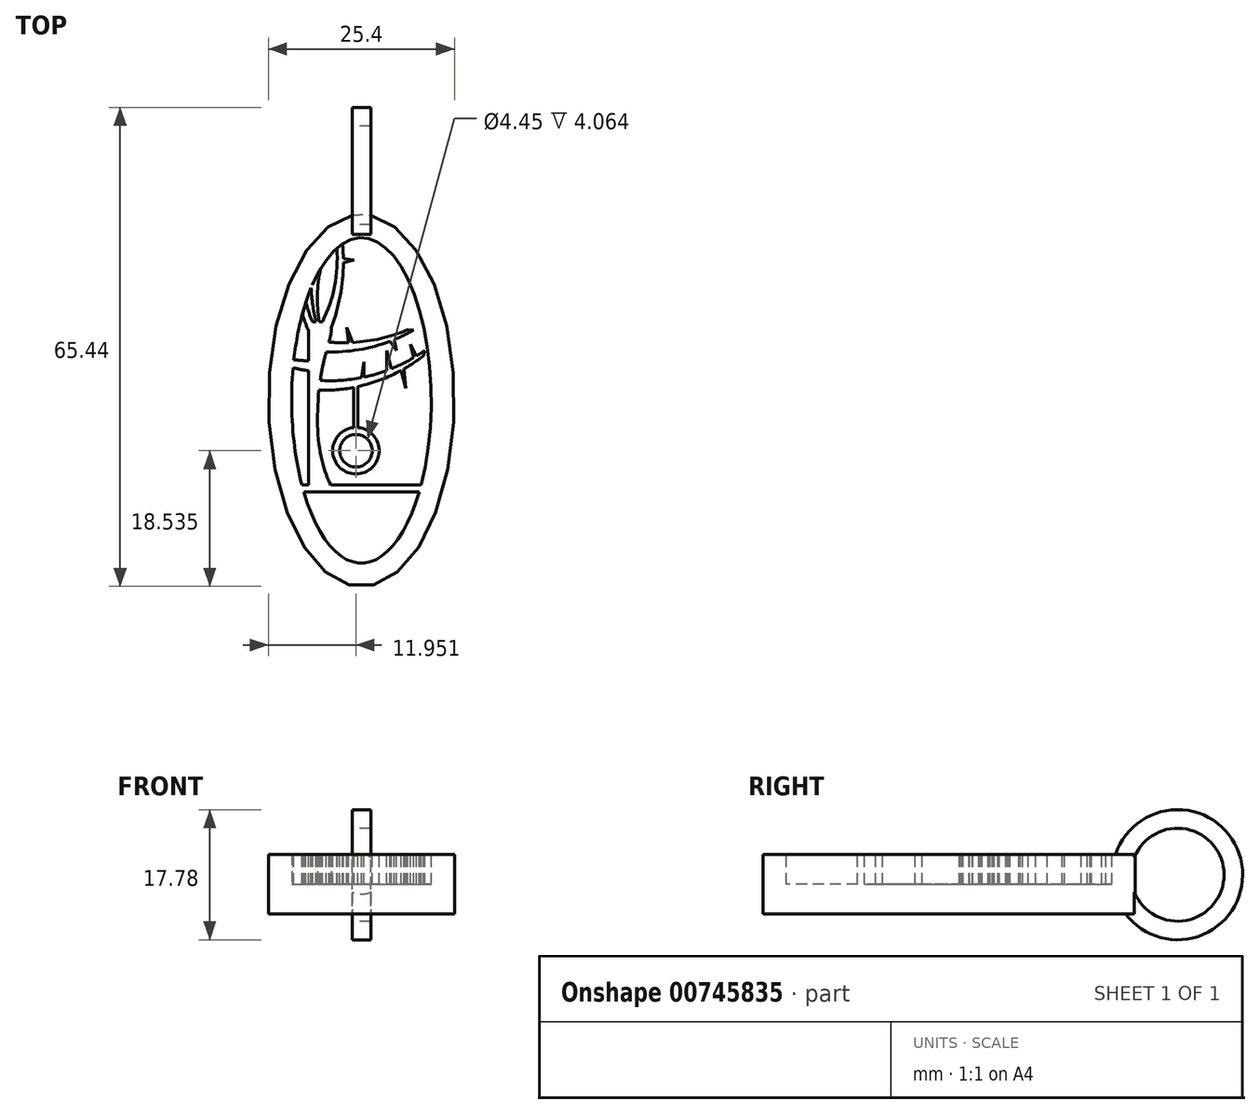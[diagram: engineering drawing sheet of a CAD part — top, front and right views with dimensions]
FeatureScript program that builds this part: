
annotation { "Feature Type Name" : "Feature", "Feature Type Description" : "" }
export const myFeature = defineFeature(function(context is Context, id is Id, definition is map)
    precondition{}
    {
        {
            var Q0;
            Q0=qCreatedBy(makeId("Top.planeOp"),FACE);
            var sketch = newSketch(context, id + "F0", { "sketchPlane" : qUnion([Q0])});
            skEllipse(sketch, "E0", {"center": v(0, 0) * mm, "majorRadius": 25.4 * mm, "minorRadius": 12.7 * mm, "majorAxis": v(0, 1)});
            skSolve(sketch);
        }
        {
            var Q0;
            Q0=qSketchRegion(id+"F0",true);
            extrude(context, id + "F1", {"entities" : qUnion([Q0]), "endBound" : BoundingType.SYMMETRIC, "depth" : 8.13 * mm, "offsetDistance" : 25.4 * mm});
        }
        {
            var Q0;
            Q0=makeQuery(id+"F1.opExtrude","CAP_FACE",FACE,{"disambiguationData":[OSD([sQuery(id+"F0.wireOp",EDGE,"E0")])],"isStart":false});
            var sketch = newSketch(context, id + "F2", { "sketchPlane" : qUnion([Q0])});
            skEllipse(sketch, "E1", {"center": v(0, 0) * mm, "majorRadius": 22.23 * mm, "minorRadius": 9.53 * mm, "majorAxis": v(0, 1)});
            skSolve(sketch);
        }
        {
            var Q0;
            Q0=qSketchRegion(id+"F2",true);
            extrude(context, id + "F3", {"entities" : qUnion([Q0]), "operationType" : NewBodyOperationType.REMOVE, "oppositeDirection" : true, "depth" : 4.06 * mm, "offsetDistance" : 25.4 * mm});
        }
        {
            var Q0;
            Q0=makeQuery(id+"F2.imprint","IMPRINT",FACE,{"disambiguationData":[TD([[makeQuery(id+"F2.imprint","IMPRINT",EDGE,{"derivedFrom":sQuery(id+"F2.wireOp",EDGE,"E1")}),1.0]])]});
            var sketch = newSketch(context, id + "F4", { "sketchPlane" : qUnion([Q0])});
            skLineSegment(sketch, "E2", {"start": v(-7.24, 10.97) * mm, "end": v(-7.24, -11.57) * mm});
            skLineSegment(sketch, "E3", {"start": v(-7.24, -11.57) * mm, "end": v(-4.2, -11.57) * mm});
            skFitSpline(sketch, "E4", {"points": [v(-4.2, -11.57) * mm, v(-5.85, -5.45) * mm, v(-4.99, 5.96) * mm, v(-4.5, 10.63) * mm, v(-7.24, 10.97) * mm], "startDerivative": vector(-8.16, 15.39) * mm, "endDerivative": vector(-7.14, 8.4) * mm});
            skLineSegment(sketch, "E5", {"start": v(-5.8, -18.4) * mm, "end": v(-5.71, -17.72) * mm});
            skLineSegment(sketch, "E6", {"start": v(-8.52, -11.57) * mm, "end": v(8.47, -11.57) * mm});
            skLineSegment(sketch, "E7", {"start": v(-8.52, -11.57) * mm, "end": v(-8.19, -12.52) * mm});
            skLineSegment(sketch, "E8", {"start": v(-8.19, -12.52) * mm, "end": v(8.37, -12.52) * mm});
            skLineSegment(sketch, "E9", {"start": v(8.37, -12.52) * mm, "end": v(8.47, -11.57) * mm});
            skPoint(sketch, "E10", {"position": v(-5.79, 1.4) * mm});
            skLineSegment(sketch, "E11", {"start": v(-0.49, 2.6) * mm, "end": v(-0.46, -4.66) * mm});
            skLineSegment(sketch, "E12", {"start": v(-1.04, -4.66) * mm, "end": v(-1.04, 2.05) * mm});
            skCircle(sketch, "E13", {"center": v(-0.75, -6.86) * mm, "radius": 3.18 * mm});
            skPoint(sketch, "E13.third.point", {"position": v(0.65, -9.72) * mm});
            skCircle(sketch, "E14", {"center": v(-0.75, -6.86) * mm, "radius": 2.22 * mm});
            skArc(sketch, "E15", {"start": v(-5.79, 1.4) * mm, "mid": v(1.75, 2.5) * mm, "end": v(8.47, 6.1) * mm});
            skArc(sketch, "E16", {"start": v(-5.62, 2.74) * mm, "mid": v(1.85, 3.56) * mm, "end": v(8.63, 6.81) * mm});
            skLineSegment(sketch, "E17", {"start": v(8.63, 6.81) * mm, "end": v(8.47, 6.1) * mm});
            skArc(sketch, "E18", {"start": v(-4.8, 6.65) * mm, "mid": v(1.38, 7.3) * mm, "end": v(7.14, 9.63) * mm});
            skArc(sketch, "E19", {"start": v(-4.63, 8) * mm, "mid": v(0.94, 8.15) * mm, "end": v(6.3, 9.67) * mm});
            skLineSegment(sketch, "E20", {"start": v(6.3, 9.67) * mm, "end": v(7.14, 9.63) * mm});
            skArc(sketch, "E21.MirrorCS", {"start": v(-7.1, 5.4) * mm, "mid": v(-8.23, 5.47) * mm, "end": v(-9.36, 5.59) * mm});
            skArc(sketch, "E22.MirrorCS", {"start": v(-7.12, 4.05) * mm, "mid": v(-8.3, 4.24) * mm, "end": v(-9.48, 4.5) * mm});
            skLineSegment(sketch, "E23", {"start": v(-9.48, 4.5) * mm, "end": v(-9.36, 5.59) * mm});
            skLineSegment(sketch, "E24", {"start": v(7.16, 5.86) * mm, "end": v(6.72, 7.71) * mm});
            skLineSegment(sketch, "E25", {"start": v(6.72, 7.71) * mm, "end": v(7.5, 6.06) * mm});
            skLineSegment(sketch, "E26", {"start": v(0, 7) * mm, "end": v(2.77, 7.7) * mm});
            skLineSegment(sketch, "E27", {"start": v(5.8, 4.3) * mm, "end": v(6.06, 1.66) * mm});
            skLineSegment(sketch, "E28", {"start": v(6.06, 1.66) * mm, "end": v(5.44, 4.11) * mm});
            skLineSegment(sketch, "E29", {"start": v(4.08, 4.33) * mm, "end": v(3.46, 6.8) * mm});
            skLineSegment(sketch, "E30", {"start": v(3.46, 6.8) * mm, "end": v(3.46, 4.1) * mm});
            skLineSegment(sketch, "E31", {"start": v(0.35, 3.2) * mm, "end": v(0.35, 5.3) * mm});
            skLineSegment(sketch, "E32", {"start": v(0.35, 5.3) * mm, "end": v(0, 3.2) * mm});
            skLineSegment(sketch, "E33", {"start": v(0, 3.2) * mm, "end": v(0, 3.12) * mm});
            skLineSegment(sketch, "E34", {"start": v(-1.74, 7.9) * mm, "end": v(-2, 9.97) * mm});
            skLineSegment(sketch, "E35", {"start": v(-2, 9.97) * mm, "end": v(-1.2, 7.92) * mm});
            skLineSegment(sketch, "E36", {"start": v(3.9, 8.08) * mm, "end": v(4.82, 6.8) * mm});
            skLineSegment(sketch, "E37", {"start": v(4.82, 6.8) * mm, "end": v(4.45, 8.3) * mm});
            skArc(sketch, "E38", {"start": v(-4.11, 9.98) * mm, "mid": v(-2.7, 15.6) * mm, "end": v(-2.58, 21.38) * mm});
            skArc(sketch, "E39", {"start": v(-5.34, 10.75) * mm, "mid": v(-3.66, 15.63) * mm, "end": v(-3.37, 20.78) * mm});
            skLineSegment(sketch, "E40", {"start": v(-3.37, 20.78) * mm, "end": v(-2.58, 21.38) * mm});
            skLineSegment(sketch, "E41", {"start": v(-2.82, 14.77) * mm, "end": v(-2.5, 17.92) * mm});
            skLineSegment(sketch, "E42", {"start": v(-2.47, 18.8) * mm, "end": v(-0.98, 19.22) * mm});
            skLineSegment(sketch, "E43", {"start": v(-0.98, 19.22) * mm, "end": v(-2.47, 19.39) * mm});
            skPoint(sketch, "E44", {"position": v(-2.66, 16.34) * mm});
            skArc(sketch, "E45.MirrorCS", {"start": v(-6.68, 10.75) * mm, "mid": v(-7.17, 12.05) * mm, "end": v(-7.57, 13.37) * mm});
            skArc(sketch, "E46.MirrorCS", {"start": v(-7.24, 9.52) * mm, "mid": v(-7.66, 10.64) * mm, "end": v(-8.04, 11.77) * mm});
            skLineSegment(sketch, "E47.MirrorCS", {"start": v(-7.57, 13.37) * mm, "end": v(-8.04, 11.77) * mm});
            skArc(sketch, "E48.MirrorCS", {"start": v(-5.75, 10.75) * mm, "mid": v(-6.01, 14.4) * mm, "end": v(-5.56, 18.03) * mm});
            skArc(sketch, "E49.MirrorCS", {"start": v(-6.22, 10.75) * mm, "mid": v(-6.66, 13.08) * mm, "end": v(-6.87, 15.44) * mm});
            skLineSegment(sketch, "E50.MirrorCS", {"start": v(-5.56, 18.03) * mm, "end": v(-6.87, 15.44) * mm});
            skSolve(sketch);
        }
        {
            var Q0;
            Q0=qSketchRegion(id+"F4",true);
            extrude(context, id + "F5", {"entities" : qUnion([Q0]), "operationType" : NewBodyOperationType.ADD, "oppositeDirection" : true, "depth" : 4.06 * mm, "offsetDistance" : 25.4 * mm});
        }
        {
            var Q0;
            Q0=qCreatedBy(makeId("Right.planeOp"),FACE);
            var sketch = newSketch(context, id + "F6", { "sketchPlane" : qUnion([Q0])});
            skCircle(sketch, "E51", {"center": v(31.15, 1.27) * mm, "radius": 6.35 * mm});
            skCircle(sketch, "E52", {"center": v(31.15, 1.27) * mm, "radius": 8.9 * mm});
            skSolve(sketch);
        }
        {
            var Q0;
            Q0 = qSketchRegion(id + "F6", true);
            extrude(context, id + "F7", {"entities" : qUnion([Q0]), "operationType" : NewBodyOperationType.ADD, "endBound" : BoundingType.SYMMETRIC, "depth" : 2.54 * mm, "offsetDistance" : 25.4 * mm});
        }
    });
